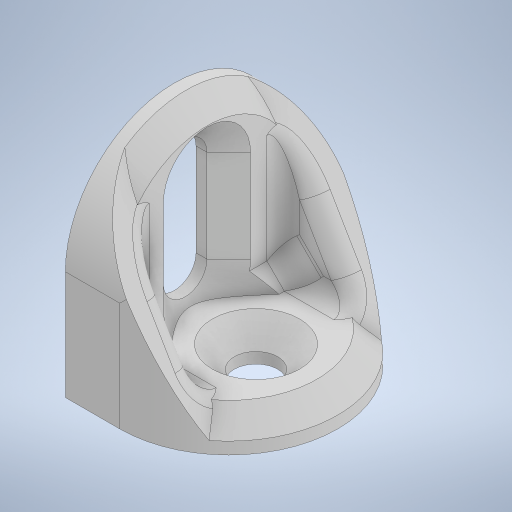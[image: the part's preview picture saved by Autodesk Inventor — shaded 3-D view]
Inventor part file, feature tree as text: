
AUTODESK INVENTOR PART (.ipt)
format: ipt  version: 2024.1 (Build 281209000, 209)  size: 475,136 bytes
history: native  units: in
note: dims shown in document units (in); Inventor stores cm internally (conversion verified against a paired STEP export)
features: extrude x5, sketch x5, fillet x3, chamfer x3, plane x2, other x1, mirror x1, projected_geometry x1
ambient origin geometry x8: Origin, YZ Plane, XZ Plane, XY Plane, X Axis, Y Axis, Z Axis, Center Point
bodies: Body1 (feature_tree)
feature tree (21):
  other  "bracket"
  extrude  "Extrusion1"  Depth=0.5906in
  extrude  "Extrusion2"  Depth=0.1181in
  extrude  "Extrusion3"  Depth=0.1575in
  extrude  "Extrusion4"  Depth=0.3937in
  plane  "Work Plane1"
  extrude  "Extrusion5"  Depth=0.2953in
  plane  "Work Plane3"
  mirror  "Mirror3"
  fillet  "Fillet1"  Radius=1.063in
  fillet  "Fillet2"  Radius=0.1575in
  fillet  "Fillet3"  Radius=0.7874in
  chamfer  "Chamfer2"  Distance=0.3937in
  chamfer  "Chamfer3"  Distance=0.7874in
  chamfer  "Chamfer4"  Distance=0.3937in
  sketch  "Sketch1"  dims[d0=0.7874in d1=0.5906in]
  sketch  "Sketch2"  dims[d2=0.1181in d3=0.0in d4=0.1181in]
  sketch  "Sketch3"  dims[d5=0.6693in d6=0.0in d7=0.1575in]
  sketch  "Sketch4"  dims[d8=0.7874in d9=0.3937in]
  sketch  "Sketch7"  dims[d12=0.5906in d13=0.2953in d14=1.063in d15=0.0in d16=0.1575in d17=0.7874in d18=0.3937in d19=0.7874in d20=0.3937in d21=1.063in d22=0.0in d27=0.0in d28=0.1969in d29=0.1969in d30=0.1181in d31=0.0in d32=0.3937in d36=0.0669in d37=0.0591in d38=0.0748in d39=0.0787in d40=45.0deg d56=0.2165in d57=0.2362in d58=0.0787in d59=0.0787in d60=45.0deg d61=0.063in d62=0.0787in d63=45.0deg]
  projected_geometry  "Projected Loop1"
